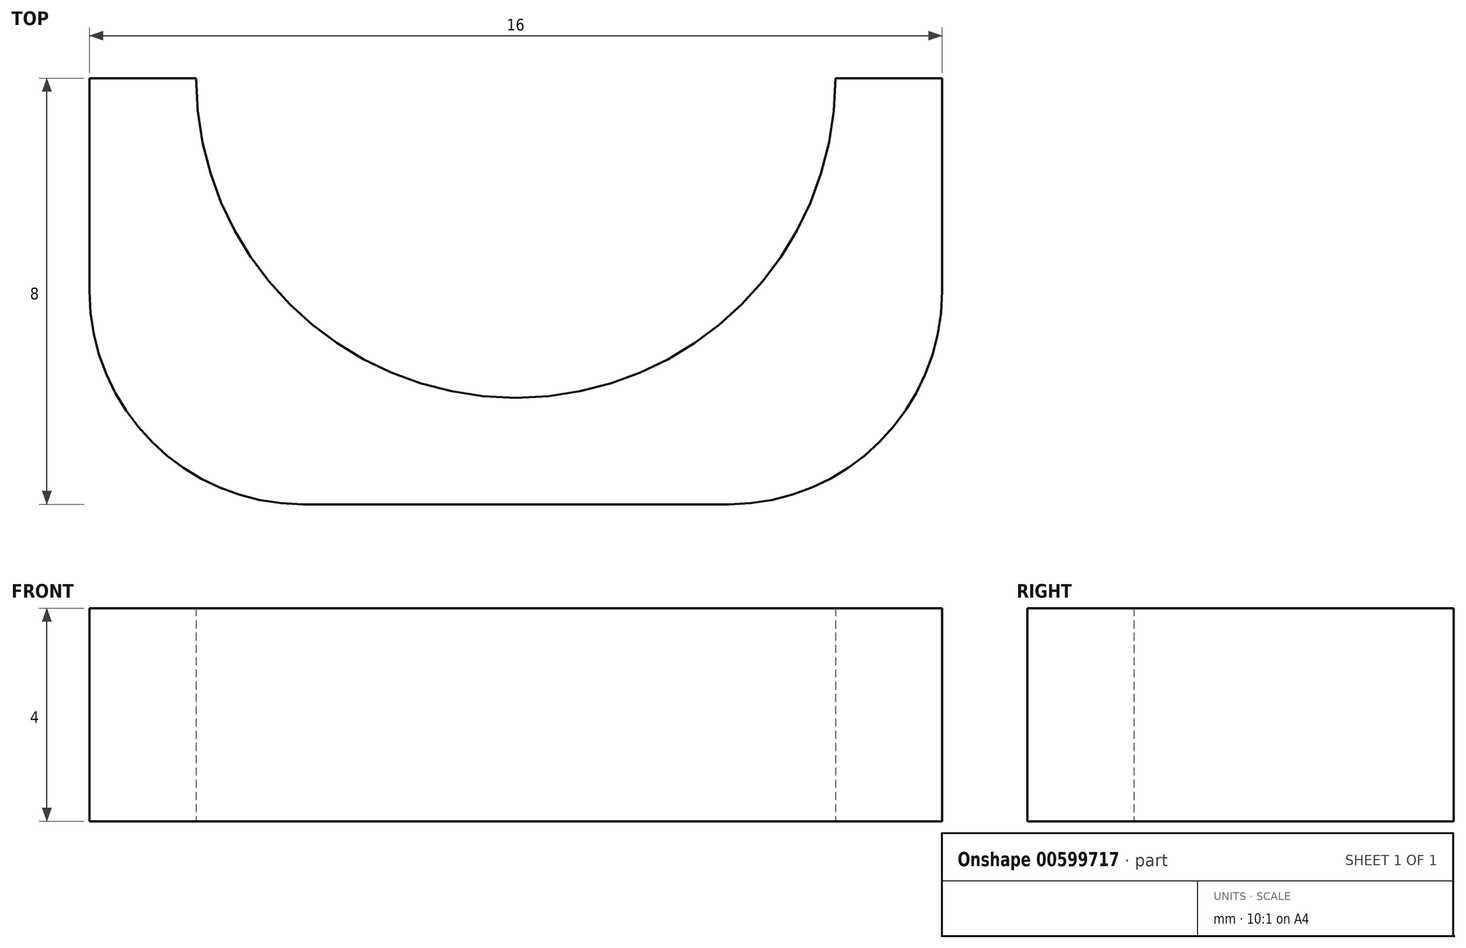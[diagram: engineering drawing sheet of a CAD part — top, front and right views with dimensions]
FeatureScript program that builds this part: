
annotation { "Feature Type Name" : "Feature", "Feature Type Description" : "" }
export const myFeature = defineFeature(function(context is Context, id is Id, definition is map)
    precondition{}
    {
        {
            var Q0;
            Q0=qCreatedBy(makeId("Top.planeOp"),FACE);
            var sketch = newSketch(context, id + "F0", { "sketchPlane" : qUnion([Q0])});
            skLineSegment(sketch, "E0.bottom", {"start": v(0, 0) * mm, "end": v(16, 0) * mm});
            skLineSegment(sketch, "E0.top", {"start": v(0, 8) * mm, "end": v(2, 8) * mm});
            skLineSegment(sketch, "E0.left", {"start": v(0, 0) * mm, "end": v(0, 8) * mm});
            skLineSegment(sketch, "E0.right", {"start": v(16, 0) * mm, "end": v(16, 8) * mm});
            skPoint(sketch, "E1", {"position": v(8, 8) * mm});
            skArc(sketch, "E2", {"start": v(2, 8) * mm, "mid": v(8, 2) * mm, "end": v(14, 8) * mm});
            skLineSegment(sketch, "E3.trimOffspring", {"start": v(14, 8) * mm, "end": v(16, 8) * mm});
            skSolve(sketch);
        }
        {
            var Q0;
            Q0=makeQuery(id+"F0.imprint","IMPRINT",FACE,{"disambiguationData":[TD([[makeQuery(id+"F0.imprint","IMPRINT",EDGE,{"derivedFrom":sQuery(id+"F0.wireOp",EDGE,"E0.bottom")}),1.0]])]});
            extrude(context, id + "F1", {"entities" : qUnion([Q0]), "depth" : 4 * mm, "offsetDistance" : 25 * mm});
        }
        {
            var Q0;
            Q0=makeQuery(id+"F1.opExtrude","SWEPT_EDGE",EDGE,{"disambiguationData":[OSD([sQuery(id+"F0.wireOp",EDGE,"E0.bottom"),sQuery(id+"F0.wireOp",EDGE,"E0.right")])]});
            var Q1;
            Q1=makeQuery(id+"F1.opExtrude","SWEPT_EDGE",EDGE,{"disambiguationData":[OSD([sQuery(id+"F0.wireOp",EDGE,"E0.bottom"),sQuery(id+"F0.wireOp",EDGE,"E0.left")])]});
            fillet(context, id + "F2", {"entities" : qUnion([Q0, Q1]), "radius" : 4 * mm, "tangentPropagation" : true, "allowEdgeOverflow" : false});
        }
    });
